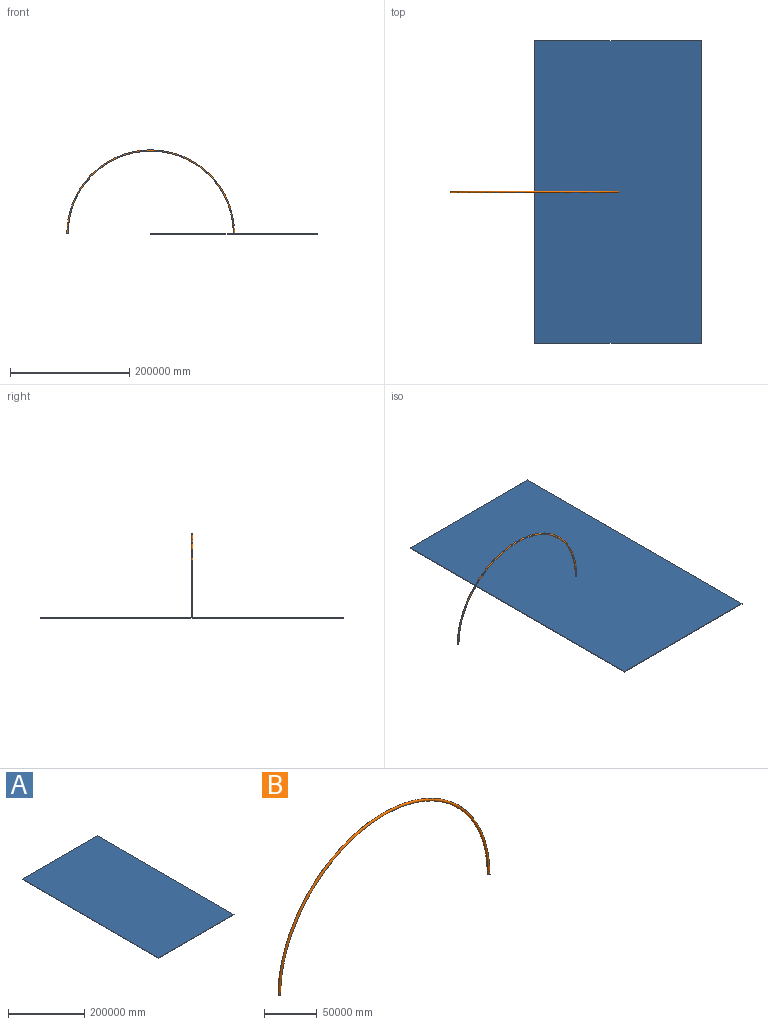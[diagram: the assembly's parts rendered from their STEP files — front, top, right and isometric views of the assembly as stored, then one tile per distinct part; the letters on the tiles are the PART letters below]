
ASSEMBLY  parts=2 mates=1
PART A: 6 faces, bbox 279400x508000x1000 mm
  f0: plane 279400x1000mm, normal (0,-1,0), area 279400000mm2, adj f1,f3,f4,f5
  f1: plane 508000x1000mm, normal (1,0,0), area 508000000mm2, adj f0,f2,f4,f5
  f2: plane 279400x1000mm, normal (0,1,0), area 279400000mm2, adj f1,f3,f4,f5
  f3: plane 508000x1000mm, normal (-1,0,0), area 508000000mm2, adj f0,f2,f4,f5
  f4: plane 508000x279400mm, normal (0,0,1), area 141935200000mm2, adj f0,f1,f2,f3
  f5: plane 508000x279400mm, normal (0,0,-1), area 141935200000mm2, adj f0,f1,f2,f3
PART B: 4 faces, bbox 305169.7x2540x152584.8 mm
  f0: torus R=139700mm, axis (0,-1,0), area 2801688549.2mm2, adj f2,f3
  f1: torus R=139700mm, axis (0,-1,0), area 3502110686.5mm2, adj f2,f3
  f2: plane 2540x2540mm, normal (0,0,-1), area 1824146.9mm2, adj f0,f1
  f3: plane 2540x2540mm, normal (0,0,-1), area 1824146.9mm2, adj f0,f1
PLACE A t=(22860.96,9987.46,2373.88)mm
PLACE B t=(-116839.04,9987.46,3373.88)mm
MATE fastened B.f2 <-> A.f4  axis (0,0,-1) through (22860.96,9987.46,3373.88)mm
